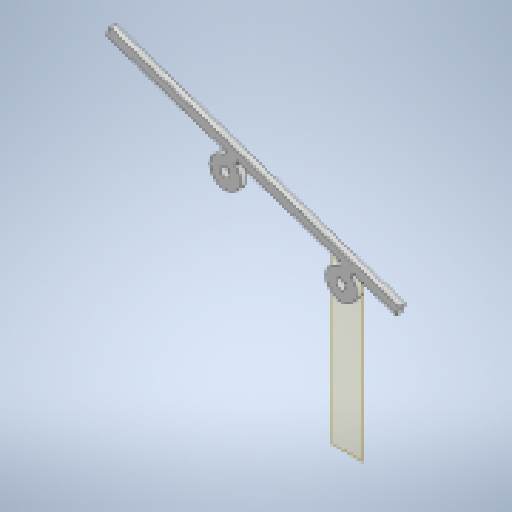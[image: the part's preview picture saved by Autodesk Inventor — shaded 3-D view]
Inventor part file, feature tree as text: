
AUTODESK INVENTOR PART (.ipt)
format: ipt  version: 2024.1 (Build 281209000, 209)  size: 198,144 bytes
history: native  units: mm
features: other x3, reference x2, plane x1, extrude x1, sketch x1
ambient origin geometry x8: Origin, YZ Plane, XZ Plane, XY Plane, X Axis, Y Axis, Z Axis, Center Point
bodies: Solid1 (feature_tree)
feature tree (8):
  plane  "Work Plane1"
  extrude  "Extrusion1"  Depth=10.0mm
  sketch  "Sketch1"  dims[d0=10.0mm d1=18.0mm d2=3.0mm d3=3.0mm d4=100.0mm d5=32.0mm d6=4.0mm d7=2.0mm d8=0.0mm d9=20.0mm d11=10.0mm d12=90.0mm d14=10.0mm d17=90.0mm d19=10.0mm d20=20.0mm d22=10.0mm]
  reference  "Reference1"
  reference  "Reference2"
  other  "<userpath>\Documents\0004-CAD\3D-cad-main\the-artifact\artifact-assembly.iam"
  other  "artifact-assembly.iam"
  other  "see-saw-arm:1"
